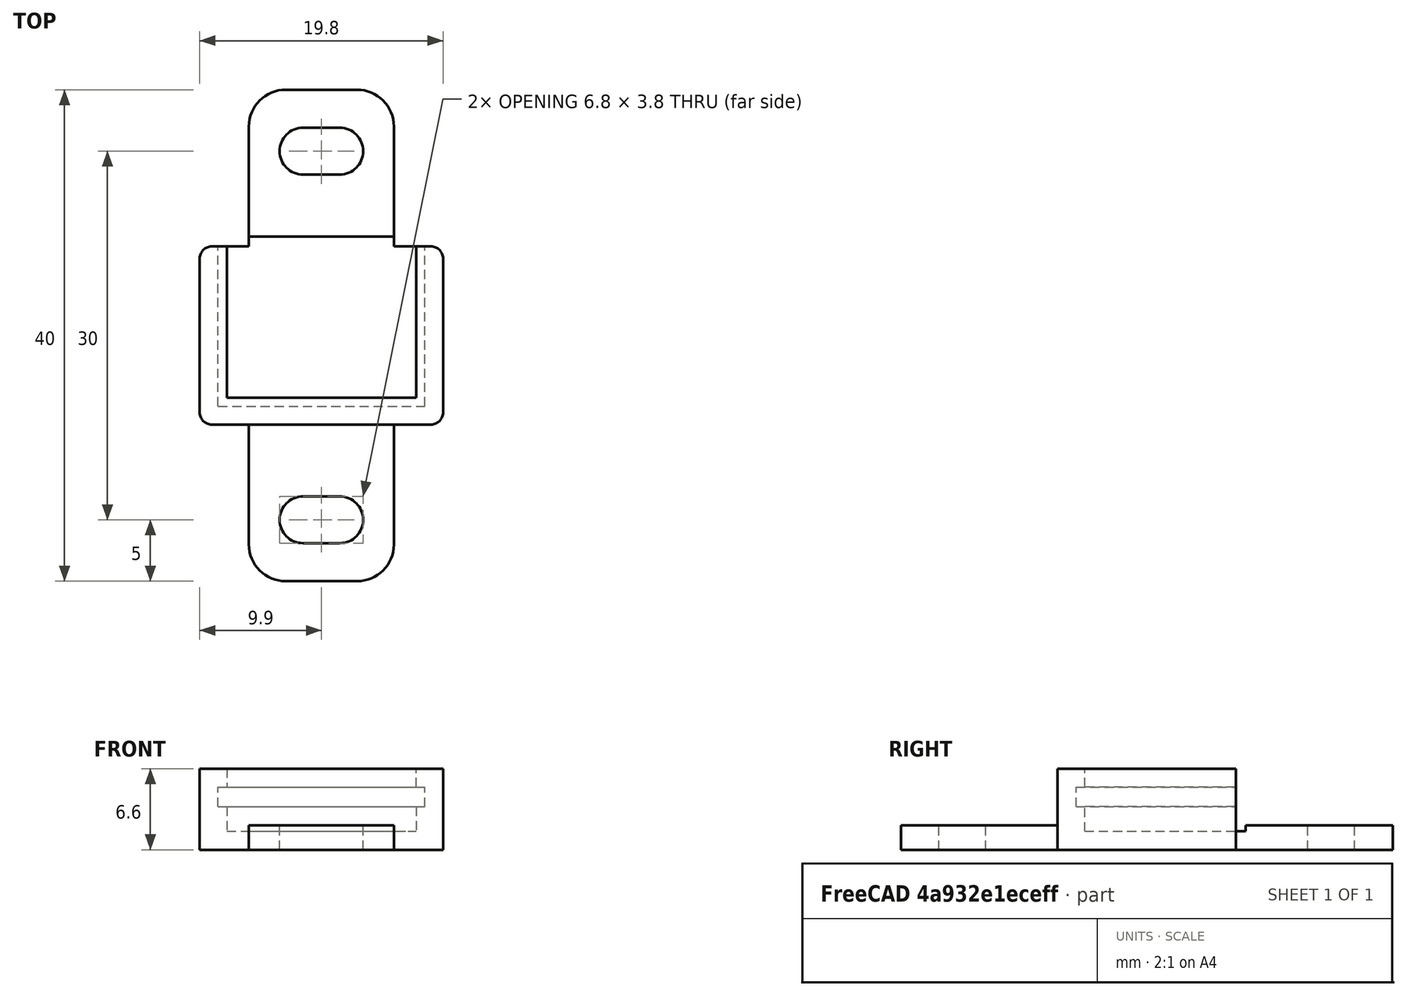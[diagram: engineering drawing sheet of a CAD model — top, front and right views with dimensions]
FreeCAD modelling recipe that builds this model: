
FCSTD DOCUMENT  (FreeCAD 0.19R23578 (Git))
Label: level_shifter
License: FreeArt
LicenseURL: http://artlibre.org/licence/lal
objects: Part::Box×3, Part::MultiFuse×2, Spreadsheet::Sheet×1, Part::Fillet×1, Part::Feature×1, Part::Cut×1, App::Part×1
note: 8 computed .brp shape members not serialized (recipe doc carries the construction recipe); baked Part::Feature solids carry a one-line shape summary decoded from their .brp

FEATURE [Spreadsheet::Sheet] Spreadsheet  label="p"
  cells = A1=pcb_x; B1(pcb_x)=16.8; A2=pcb_y; B2(pcb_y)=13; A3=pcb_z; B3(pcb_z)=1.6; A4=pcb_under; B4(pcb_under)=2; A5=side_wall; B5(side_wall)=1.5; A6=pcb_side_lane; B6(pcb_side_lane)=0.7; A7=bottom_wall; B7(bottom_wall)=1.5; A8=pcb_above; B8(pcb_above)=1.5
FEATURE [Part::Box] Box  label="external cube"
  AttacherType = Attacher::AttachEngine3D
  Height = 6.6
  Length = 19.8
  Width = 14.5
  expr: Height = <<p>>.bottom_wall + <<p>>.pcb_under + <<p>>.pcb_z + <<p>>.pcb_above
  expr: Width = <<p>>.pcb_y + <<p>>.side_wall
  expr: Length = <<p>>.pcb_x + 2 * <<p>>.side_wall
FEATURE [Part::Box] Box006  label="internal cube"
  AttacherType = Attacher::AttachEngine3D
  Height = 5.1
  Length = 15.4
  Placement = pos=(2.2,2.2,1.5) rot=(0,0,1;0rad)
  Width = 13.1
  expr: .Placement.Base.y = <<p>>.side_wall + <<p>>.pcb_side_lane
  expr: .Placement.Base.x = <<p>>.side_wall + <<p>>.pcb_side_lane
  expr: .Placement.Base.z = <<p>>.bottom_wall
  expr: Height = <<p>>.pcb_under + <<p>>.pcb_z + <<p>>.pcb_above
  expr: Width = <<p>>.pcb_y - 2 * <<p>>.pcb_side_lane + <<p>>.side_wall
  expr: Length = <<p>>.pcb_x - 2 * <<p>>.pcb_side_lane
FEATURE [Part::Box] Box007  label="pcb extract cube"
  AttacherType = Attacher::AttachEngine3D
  Height = 1.6
  Length = 16.8
  Placement = pos=(1.5,1.5,3.5) rot=(0,0,1;0rad)
  Width = 13
  expr: .Placement.Base.y = <<p>>.side_wall
  expr: .Placement.Base.x = <<p>>.side_wall
  expr: Length = <<p>>.pcb_x
  expr: Width = <<p>>.pcb_y
  expr: .Placement.Base.z = <<p>>.bottom_wall + <<p>>.pcb_under
  expr: Height = <<p>>.pcb_z
FEATURE [Part::MultiFuse] Fusion  label="extract fusion"
  Shapes = -> [Box006,Box007]
FEATURE [Part::Fillet] Fillet  label="external fillet"
  Base = -> Box
  Edges = 4 edges r=1: [Edge1,Edge3,Edge5,Edge7]
FEATURE [Part::Feature] Cut002001  label="attach plane y dir001"
  Placement = pos=(4,-12.75,0) rot=(0,0,1;0rad)
  shape: bbox 11.8 x 40 x 2 mm, 20 faces (baked)
FEATURE [Part::MultiFuse] Fusion001  label="body fusion"
  Shapes = -> [Fillet,Cut002001]
FEATURE [Part::Cut] Cut  label="body cut"
  Base = -> Fusion001
  Tool = -> Fusion
FEATURE [App::Part] Part  label="buzzer pcb box part"
  Group = -> [Box,Fillet,Fusion001,Fusion,Box007,Box006,Cut]
  Origin = -> Origin
